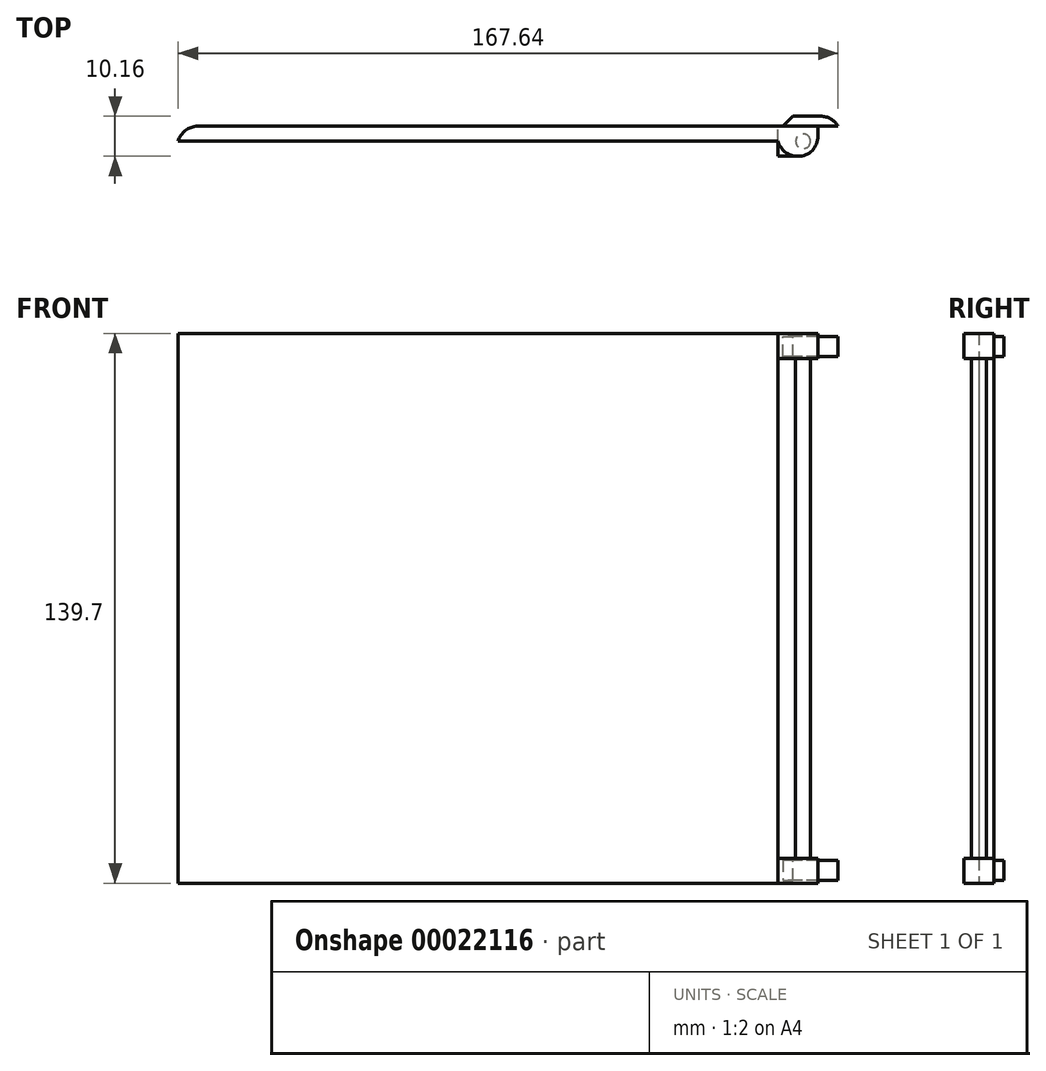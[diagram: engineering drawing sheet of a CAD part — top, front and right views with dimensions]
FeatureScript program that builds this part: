
annotation { "Feature Type Name" : "Feature", "Feature Type Description" : "" }
export const myFeature = defineFeature(function(context is Context, id is Id, definition is map)
    precondition{}
    {
        {
            var Q0;
            Q0=qCreatedBy(makeId("Front.planeOp"),FACE);
            var sketch = newSketch(context, id + "F0", { "sketchPlane" : qUnion([Q0])});
            skLineSegment(sketch, "E0.bottom", {"start": v(0, 93.72) * mm, "end": v(-152.4, 93.72) * mm});
            skLineSegment(sketch, "E0.top", {"start": v(0, -45.98) * mm, "end": v(-152.4, -45.98) * mm});
            skLineSegment(sketch, "E0.left", {"start": v(0, 87.37) * mm, "end": v(0, -39.63) * mm});
            skLineSegment(sketch, "E0.right", {"start": v(-152.4, 93.72) * mm, "end": v(-152.4, -45.98) * mm});
            skLineSegment(sketch, "E1.bottom", {"start": v(0, 93.72) * mm, "end": v(10.16, 93.72) * mm});
            skLineSegment(sketch, "E1.top", {"start": v(0, 87.37) * mm, "end": v(10.16, 87.37) * mm});
            skLineSegment(sketch, "E1.right", {"start": v(10.16, 93.72) * mm, "end": v(10.16, 87.37) * mm});
            skLineSegment(sketch, "E2.bottom", {"start": v(0, -45.98) * mm, "end": v(10.16, -45.98) * mm});
            skLineSegment(sketch, "E2.top", {"start": v(0, -39.63) * mm, "end": v(10.16, -39.63) * mm});
            skLineSegment(sketch, "E2.right", {"start": v(10.16, -45.98) * mm, "end": v(10.16, -39.63) * mm});
            skSolve(sketch);
        }
        {
            var Q0;
            Q0=makeQuery(id+"F0.imprint","IMPRINT",FACE,{"disambiguationData":[TD([[makeQuery(id+"F0.imprint","IMPRINT",EDGE,{"derivedFrom":sQuery(id+"F0.wireOp",EDGE,"E0.bottom")}),1.0]])]});
            extrude(context, id + "F1", {"entities" : qUnion([Q0]), "depth" : 7.62 * mm});
        }
        {
            var Q0;
            Q0=makeQuery(id+"F1.opExtrude","SWEPT_FACE",FACE,{"disambiguationData":[OSD([sQuery(id+"F0.wireOp",EDGE,"E2.top")])]});
            var sketch = newSketch(context, id + "F2", { "sketchPlane" : qUnion([Q0])});
            skCircle(sketch, "E3", {"center": v(6.35, -3.81) * mm, "radius": 1.88 * mm});
            skLineSegment(sketch, "E4", {"start": v(6.35, -3.81) * mm, "end": v(10.16, -3.81) * mm});
            skSolve(sketch);
        }
        {
            var Q0;
            Q0=makeQuery(id+"F2.imprint","IMPRINT",FACE,{"disambiguationData":[TD([[makeQuery(id+"F2.imprint","IMPRINT",EDGE,{"derivedFrom":sQuery(id+"F2.wireOp",EDGE,"E3")}),1.0]])]});
            extrude(context, id + "F3", {"entities" : qUnion([Q0]), "operationType" : NewBodyOperationType.ADD, "depth" : 127 * mm});
        }
        {
            var Q0;
            Q0=makeQuery(id+"F1.opExtrude","CAP_FACE",FACE,{"disambiguationData":[OSD([sQuery(id+"F0.wireOp",EDGE,"E0.bottom"),sQuery(id+"F0.wireOp",EDGE,"E0.top"),sQuery(id+"F0.wireOp",EDGE,"E0.left"),sQuery(id+"F0.wireOp",EDGE,"E0.right"),sQuery(id+"F0.wireOp",EDGE,"E1.bottom"),sQuery(id+"F0.wireOp",EDGE,"E1.top"),sQuery(id+"F0.wireOp",EDGE,"E1.right"),sQuery(id+"F0.wireOp",EDGE,"E2.bottom"),sQuery(id+"F0.wireOp",EDGE,"E2.top"),sQuery(id+"F0.wireOp",EDGE,"E2.right")])],"isStart":false});
            var sketch = newSketch(context, id + "F4", { "sketchPlane" : qUnion([Q0])});
            skLineSegment(sketch, "E5.bottom", {"start": v(0, 93.72) * mm, "end": v(-152.4, 93.72) * mm});
            skLineSegment(sketch, "E5.top", {"start": v(0, -45.98) * mm, "end": v(-152.4, -45.98) * mm});
            skLineSegment(sketch, "E5.left", {"start": v(0, 93.72) * mm, "end": v(0, -45.98) * mm});
            skLineSegment(sketch, "E5.right", {"start": v(-152.4, 93.72) * mm, "end": v(-152.4, -45.98) * mm});
            skSolve(sketch);
        }
        {
            var Q0;
            {var subQ3=sQuery(id+"F4.wireOp",EDGE,"E5.bottom");Q0=makeQuery(id+"F4.imprint","IMPRINT",FACE,{"disambiguationData":[TD([[makeQuery(id+"F4.imprint","IMPRINT",EDGE,{"derivedFrom":subQ3}),-1.0]])]});}
            extrude(context, id + "F5", {"entities" : qUnion([Q0]), "operationType" : NewBodyOperationType.REMOVE, "oppositeDirection" : true, "depth" : 3.8 * mm});
        }
        {
            var Q0;
            Q0=makeQuery(id+"F5.boolean.opBoolean","COPY",EDGE,{"disambiguationData":[OD(0.0)],"derivedFrom":makeQuery(id+"F5.opExtrude","CAP_EDGE",EDGE,{"disambiguationData":[OSD([sQuery(id+"F4.wireOp",EDGE,"E5.left")])],"isStart":true})});
            var Q1;
            Q1=makeQuery(id+"F1.opExtrude","CAP_EDGE",EDGE,{"disambiguationData":[OSD([sQuery(id+"F0.wireOp",EDGE,"E1.right")])],"isStart":false});
            var Q2;
            Q2=makeQuery(id+"F5.boolean.opBoolean","COPY",EDGE,{"disambiguationData":[OD(1.0)],"derivedFrom":makeQuery(id+"F5.opExtrude","CAP_EDGE",EDGE,{"disambiguationData":[OSD([sQuery(id+"F4.wireOp",EDGE,"E5.left")])],"isStart":true})});
            var Q3;
            Q3=makeQuery(id+"F1.opExtrude","CAP_EDGE",EDGE,{"disambiguationData":[OSD([sQuery(id+"F0.wireOp",EDGE,"E2.right")])],"isStart":false});
            fillet(context, id + "F6", {"entities" : qUnion([Q0, Q1, Q2, Q3]), "radius" : 5.08 * mm, "tangentPropagation" : true, "allowEdgeOverflow" : false});
        }
        {
            var Q0;
            Q0=makeQuery(id+"F1.opExtrude","CAP_FACE",FACE,{"disambiguationData":[OSD([sQuery(id+"F0.wireOp",EDGE,"E0.bottom"),sQuery(id+"F0.wireOp",EDGE,"E0.top"),sQuery(id+"F0.wireOp",EDGE,"E0.left"),sQuery(id+"F0.wireOp",EDGE,"E0.right"),sQuery(id+"F0.wireOp",EDGE,"E1.bottom"),sQuery(id+"F0.wireOp",EDGE,"E1.top"),sQuery(id+"F0.wireOp",EDGE,"E1.right"),sQuery(id+"F0.wireOp",EDGE,"E2.bottom"),sQuery(id+"F0.wireOp",EDGE,"E2.top"),sQuery(id+"F0.wireOp",EDGE,"E2.right")])],"isStart":true});
            var sketch = newSketch(context, id + "F7", { "sketchPlane" : qUnion([Q0])});
            skLineSegment(sketch, "E6.bottom", {"start": v(-10.16, 92.96) * mm, "end": v(1.27, 92.96) * mm});
            skLineSegment(sketch, "E6.top", {"start": v(-10.16, 87.88) * mm, "end": v(1.27, 87.88) * mm});
            skLineSegment(sketch, "E6.left", {"start": v(-10.16, 92.96) * mm, "end": v(-10.16, 87.88) * mm});
            skLineSegment(sketch, "E6.right", {"start": v(1.27, 92.96) * mm, "end": v(1.27, 87.88) * mm});
            skLineSegment(sketch, "E7.bottom", {"start": v(-10.16, -45.22) * mm, "end": v(1.27, -45.22) * mm});
            skLineSegment(sketch, "E7.top", {"start": v(-10.16, -40.14) * mm, "end": v(1.27, -40.14) * mm});
            skLineSegment(sketch, "E7.left", {"start": v(-10.16, -45.22) * mm, "end": v(-10.16, -40.14) * mm});
            skLineSegment(sketch, "E7.right", {"start": v(1.27, -45.22) * mm, "end": v(1.27, -40.14) * mm});
            skSolve(sketch);
        }
        {
            var Q0;
            Q0 = qSketchRegion(id + "F7", true);
            extrude(context, id + "F8", {"entities" : qUnion([Q0]), "operationType" : NewBodyOperationType.ADD, "depth" : 2.54 * mm});
        }
        {
            var Q0;
            Q0=makeQuery(id+"F8.boolean.opBoolean","MERGE",FACE,{"derivedFrom":[makeQuery(id+"F1.opExtrude","SWEPT_FACE",FACE,{"disambiguationData":[OSD([sQuery(id+"F0.wireOp",EDGE,"E2.right")])]}),makeQuery(id+"F8.opExtrude","SWEPT_FACE",FACE,{"disambiguationData":[OSD([sQuery(id+"F7.wireOp",EDGE,"E7.left")])]})]});
            var sketch = newSketch(context, id + "F9", { "sketchPlane" : qUnion([Q0])});
            skLineSegment(sketch, "E8", {"start": v(0, -40.14) * mm, "end": v(0, -45.22) * mm});
            skSolve(sketch);
        }
        {
            var Q0;
            Q0=makeQuery(id+"F8.boolean.opBoolean","MERGE",FACE,{"derivedFrom":[makeQuery(id+"F1.opExtrude","SWEPT_FACE",FACE,{"disambiguationData":[OSD([sQuery(id+"F0.wireOp",EDGE,"E1.right")])]}),makeQuery(id+"F8.opExtrude","SWEPT_FACE",FACE,{"disambiguationData":[OSD([sQuery(id+"F7.wireOp",EDGE,"E6.left")])]})]});
            var sketch = newSketch(context, id + "F10", { "sketchPlane" : qUnion([Q0])});
            skLineSegment(sketch, "E9", {"start": v(0, 92.96) * mm, "end": v(0, 87.88) * mm});
            skSolve(sketch);
        }
        {
            var Q0;
            Q0=makeQuery(id+"F10.imprint","IMPRINT",FACE,{"disambiguationData":[TD([[makeQuery(id+"F10.imprint","IMPRINT",EDGE,{"derivedFrom":sQuery(id+"F10.wireOp",EDGE,"E9")}),1.0]])]});
            var Q1;
            Q1=makeQuery(id+"F9.imprint","IMPRINT",FACE,{"disambiguationData":[TD([[makeQuery(id+"F9.imprint","IMPRINT",EDGE,{"derivedFrom":sQuery(id+"F9.wireOp",EDGE,"E8")}),1.0]])]});
            extrude(context, id + "F11", {"entities" : qUnion([Q0, Q1]), "operationType" : NewBodyOperationType.ADD, "depth" : 5.08 * mm});
        }
        {
            var Q0;
            Q0=makeQuery(id+"F8.opExtrude","CAP_EDGE",EDGE,{"disambiguationData":[OSD([sQuery(id+"F7.wireOp",EDGE,"E6.right")])],"isStart":false});
            var Q1;
            Q1=makeQuery(id+"F8.opExtrude","CAP_EDGE",EDGE,{"disambiguationData":[OSD([sQuery(id+"F7.wireOp",EDGE,"E7.right")])],"isStart":false});
            chamfer(context, id + "F12", {"entities" : qUnion([Q0, Q1]), "width" : 5.08 * mm, "tangentPropagation" : true});
        }
        {
            var Q0;
            Q0=makeQuery(id+"F11.opExtrude","CAP_EDGE",EDGE,{"disambiguationData":[OSD([sQuery(id+"F7.wireOp",EDGE,"E7.left")])],"isStart":false});
            var Q1;
            Q1=makeQuery(id+"F11.opExtrude","CAP_EDGE",EDGE,{"disambiguationData":[OSD([sQuery(id+"F7.wireOp",EDGE,"E6.left")])],"isStart":false});
            fillet(context, id + "F13", {"entities" : qUnion([Q0, Q1]), "radius" : 5.08 * mm, "tangentPropagation" : true, "allowEdgeOverflow" : false});
        }
        {
            var Q0;
            Q0=makeQuery(id+"F1.opExtrude","CAP_EDGE",EDGE,{"disambiguationData":[OSD([sQuery(id+"F0.wireOp",EDGE,"E0.right")])],"isStart":true});
            fillet(context, id + "F14", {"entities" : qUnion([Q0]), "radius" : 5.08 * mm, "tangentPropagation" : true, "allowEdgeOverflow" : false});
        }
    });
